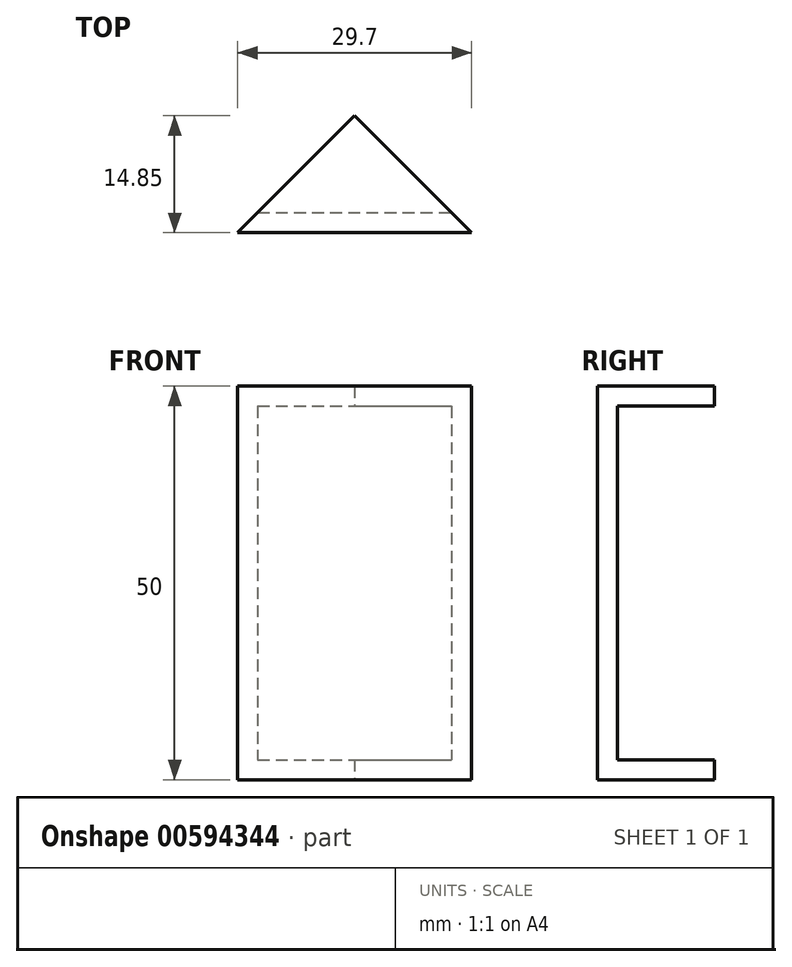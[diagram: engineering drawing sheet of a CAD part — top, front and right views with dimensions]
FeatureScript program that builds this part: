
annotation { "Feature Type Name" : "Feature", "Feature Type Description" : "" }
export const myFeature = defineFeature(function(context is Context, id is Id, definition is map)
    precondition{}
    {
        {
            var Q0;
            Q0=qCreatedBy(makeId("Top.planeOp"),FACE);
            var sketch = newSketch(context, id + "F0", { "sketchPlane" : qUnion([Q0])});
            skLineSegment(sketch, "E0", {"start": v(0, 0) * mm, "end": v(14.85, -14.85) * mm});
            skLineSegment(sketch, "E1", {"start": v(-14.85, -14.85) * mm, "end": v(14.85, -14.85) * mm});
            skLineSegment(sketch, "E2", {"start": v(-14.85, -14.85) * mm, "end": v(0, 0) * mm});
            skSolve(sketch);
        }
        {
            var Q0;
            Q0=makeQuery(id+"F0.imprint","IMPRINT",FACE,{"disambiguationData":[TD([[makeQuery(id+"F0.imprint","IMPRINT",EDGE,{"derivedFrom":sQuery(id+"F0.wireOp",EDGE,"E0")}),-1.0]])]});
            extrude(context, id + "F1", {"entities" : qUnion([Q0]), "depth" : 50 * mm, "offsetDistance" : 25.4 * mm});
        }
        {
            var Q0;
            Q0=makeQuery(id+"F1.opExtrude","SWEPT_FACE",FACE,{"disambiguationData":[OSD([sQuery(id+"F0.wireOp",EDGE,"E2")])]});
            var Q1;
            Q1=makeQuery(id+"F1.opExtrude","SWEPT_FACE",FACE,{"disambiguationData":[OSD([sQuery(id+"F0.wireOp",EDGE,"E0")])]});
            shell(context, id + "F2", {"entities" : qUnion([Q0, Q1]), "thickness" : 2.54 * mm});
        }
    });
